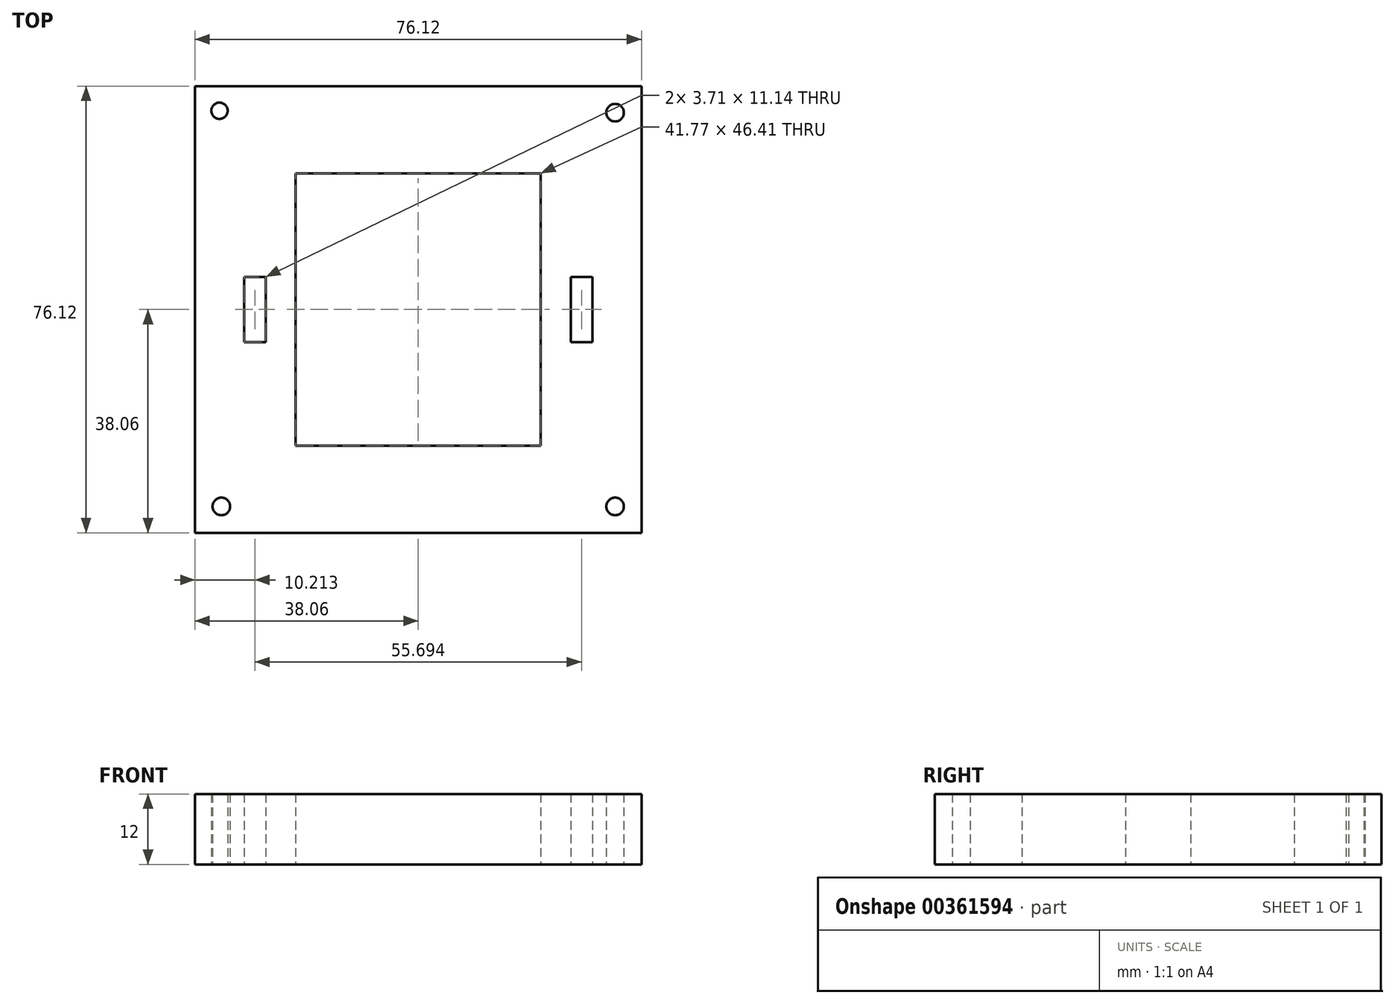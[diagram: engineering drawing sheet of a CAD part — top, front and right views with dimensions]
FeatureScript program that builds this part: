
annotation { "Feature Type Name" : "Feature", "Feature Type Description" : "" }
export const myFeature = defineFeature(function(context is Context, id is Id, definition is map)
    precondition{}
    {
        {
            var Q0;
            Q0=qCreatedBy(makeId("Top.planeOp"),FACE);
            var sketch = newSketch(context, id + "F0", { "sketchPlane" : qUnion([Q0])});
            skLineSegment(sketch, "E0.bottom", {"start": v(-20.89, 23.2) * mm, "end": v(20.89, 23.2) * mm});
            skLineSegment(sketch, "E0.top", {"start": v(-20.89, -23.2) * mm, "end": v(20.89, -23.2) * mm});
            skLineSegment(sketch, "E0.left", {"start": v(-20.89, 23.2) * mm, "end": v(-20.89, -23.2) * mm});
            skLineSegment(sketch, "E0.right", {"start": v(20.89, 23.2) * mm, "end": v(20.89, -23.2) * mm});
            skPoint(sketch, "E0.middle", {"position": v(0, 0) * mm});
            skLineSegment(sketch, "E1.bottom", {"start": v(-38.06, -38.06) * mm, "end": v(38.06, -38.06) * mm});
            skLineSegment(sketch, "E1.top", {"start": v(-38.06, 38.06) * mm, "end": v(38.06, 38.06) * mm});
            skLineSegment(sketch, "E1.left", {"start": v(-38.06, -38.06) * mm, "end": v(-38.06, 38.06) * mm});
            skLineSegment(sketch, "E1.right", {"start": v(38.06, -38.06) * mm, "end": v(38.06, 38.06) * mm});
            skLineSegment(sketch, "E2.bottom", {"start": v(29.7, -5.57) * mm, "end": v(26, -5.57) * mm});
            skLineSegment(sketch, "E2.top", {"start": v(29.7, 5.57) * mm, "end": v(26, 5.57) * mm});
            skLineSegment(sketch, "E2.left", {"start": v(29.7, -5.57) * mm, "end": v(29.7, 5.57) * mm});
            skLineSegment(sketch, "E2.right", {"start": v(26, -5.57) * mm, "end": v(26, 5.57) * mm});
            skPoint(sketch, "E2.middle", {"position": v(27.85, 0) * mm});
            skLineSegment(sketch, "E3.bottom", {"start": v(-26, -5.57) * mm, "end": v(-29.7, -5.57) * mm});
            skLineSegment(sketch, "E3.top", {"start": v(-26, 5.57) * mm, "end": v(-29.7, 5.57) * mm});
            skLineSegment(sketch, "E3.left", {"start": v(-26, -5.57) * mm, "end": v(-26, 5.57) * mm});
            skLineSegment(sketch, "E3.right", {"start": v(-29.7, -5.57) * mm, "end": v(-29.7, 5.57) * mm});
            skPoint(sketch, "E3.middle", {"position": v(-27.85, 0) * mm});
            skCircle(sketch, "E4", {"center": v(-33.88, 33.88) * mm, "radius": 1.4 * mm});
            skCircle(sketch, "E5", {"center": v(-33.56, -33.56) * mm, "radius": 1.5 * mm});
            skCircle(sketch, "E6", {"center": v(33.56, -33.56) * mm, "radius": 1.5 * mm});
            skCircle(sketch, "E7", {"center": v(33.56, 33.56) * mm, "radius": 1.5 * mm});
            skSolve(sketch);
        }
        {
            var Q0;
            Q0=makeQuery(id+"F0.imprint","IMPRINT",FACE,{"disambiguationData":[TD([[makeQuery(id+"F0.imprint","IMPRINT",EDGE,{"derivedFrom":sQuery(id+"F0.wireOp",EDGE,"E0.bottom")}),1.0]])]});
            extrude(context, id + "F1", {"entities" : qUnion([Q0]), "depth" : 12 * mm});
        }
    });
